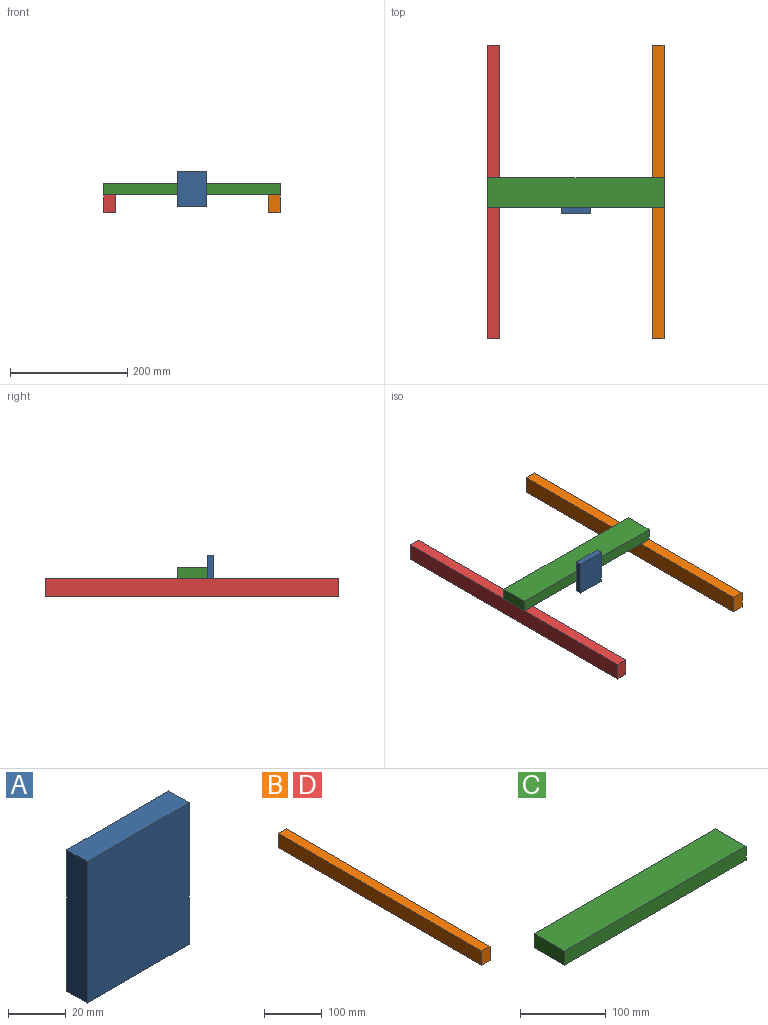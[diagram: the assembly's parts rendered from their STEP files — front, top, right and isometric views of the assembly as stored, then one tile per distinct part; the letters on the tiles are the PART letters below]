
ASSEMBLY  parts=4 mates=6
PART A: 6 faces, bbox 50x10x60 mm
  f0: plane 60x10mm, normal (1,0,0), area 600mm2, adj f1,f3,f4,f5
  f1: plane 50x10mm, normal (0,0,1), area 500mm2, adj f0,f2,f4,f5
  f2: plane 60x10mm, normal (-1,0,0), area 600mm2, adj f1,f3,f4,f5
  f3: plane 50x10mm, normal (0,0,-1), area 500mm2, adj f0,f2,f4,f5
  f4: plane 60x50mm, normal (0,-1,0), area 3000mm2, adj f0,f1,f2,f3
  f5: plane 60x50mm, normal (0,1,0), area 3000mm2, adj f0,f1,f2,f3
PART B: 6 faces, bbox 20x500x30 mm
  f0: plane 500x30mm, normal (1,0,0), area 15000mm2, adj f1,f3,f4,f5
  f1: plane 500x20mm, normal (0,0,1), area 10000mm2, adj f0,f2,f4,f5
  f2: plane 500x30mm, normal (-1,0,0), area 15000mm2, adj f1,f3,f4,f5
  f3: plane 500x20mm, normal (0,0,-1), area 10000mm2, adj f0,f2,f4,f5
  f4: plane 30x20mm, normal (0,-1,0), area 600mm2, adj f0,f1,f2,f3
  f5: plane 30x20mm, normal (0,1,0), area 600mm2, adj f0,f1,f2,f3
PART C: 6 faces, bbox 300x50x20 mm
  f0: plane 300x20mm, normal (0,1,0), area 6000mm2, adj f1,f3,f4,f5
  f1: plane 300x50mm, normal (0,0,1), area 15000mm2, adj f0,f2,f4,f5
  f2: plane 300x20mm, normal (0,-1,0), area 6000mm2, adj f1,f3,f4,f5
  f3: plane 300x50mm, normal (0,0,-1), area 15000mm2, adj f0,f2,f4,f5
  f4: plane 50x20mm, normal (1,0,0), area 1000mm2, adj f0,f1,f2,f3
  f5: plane 50x20mm, normal (-1,0,0), area 1000mm2, adj f0,f1,f2,f3
PART D: same geometry as B
PLACE A t=(-50.68,-8.14,47.12)mm
PLACE B t=(89.32,22.96,22.12)mm
PLACE C t=(-50.68,21.86,47.12)mm
PLACE D t=(-190.68,22.96,22.12)mm
MATE planar D.f4 <-> B.f4  axis (0,-1,0) through (-190.68,-227.04,22.12)mm
MATE planar C.f5 <-> D.f2  axis (-1,0,0) through (-200.68,21.86,47.12)mm
MATE planar C.f3 <-> D.f1  axis (0,0,-1) through (-50.68,21.86,37.12)mm
MATE planar C.f4 <-> B.f0  axis (1,0,0) through (99.32,21.86,47.12)mm
MATE planar C.f3 <-> B.f1  axis (0,0,-1) through (-50.68,21.86,37.12)mm
MATE planar A.f5 <-> C.f2  axis (0,1,0) through (-50.68,-3.14,47.12)mm
